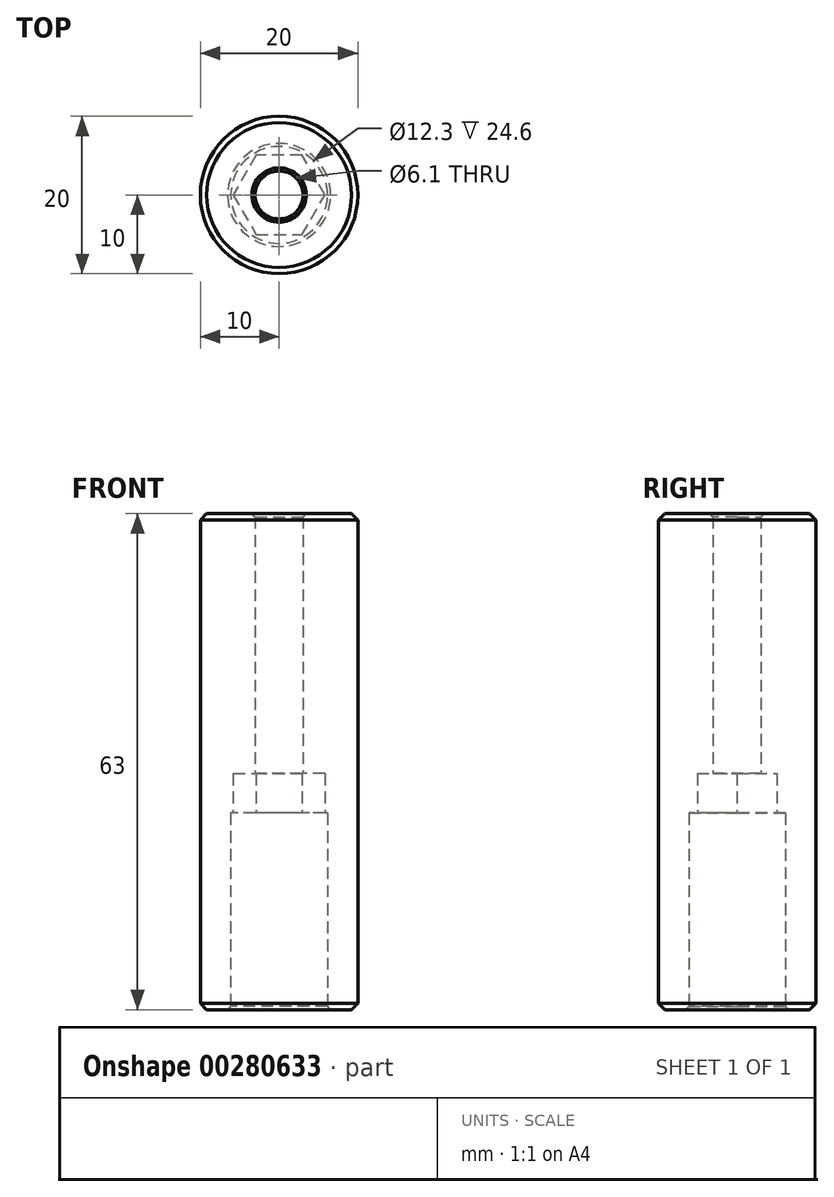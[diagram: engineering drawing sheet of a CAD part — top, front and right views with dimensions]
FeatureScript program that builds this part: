
annotation { "Feature Type Name" : "Feature", "Feature Type Description" : "" }
export const myFeature = defineFeature(function(context is Context, id is Id, definition is map)
    precondition{}
    {
        {
            var Q0;
            Q0=qCreatedBy(makeId("Top.planeOp"),FACE);
            var sketch = newSketch(context, id + "F0", { "sketchPlane" : qUnion([Q0])});
            skCircle(sketch, "E0", {"center": v(0, 0) * mm, "radius": 10 * mm});
            skCircle(sketch, "E1", {"center": v(0, 0) * mm, "radius": 6.15 * mm});
            skSolve(sketch);
        }
        {
            var Q0;
            Q0 = qSketchRegion(id + "F0", true);
            extrude(context, id + "F1", {"entities" : qUnion([Q0]), "depth" : 25 * mm});
        }
        {
            var Q0;
            Q0=makeQuery(id+"F1.opExtrude","CAP_FACE",FACE,{"disambiguationData":[OSD([sQuery(id+"F0.wireOp",EDGE,"E0"),sQuery(id+"F0.wireOp",EDGE,"E1")])],"isStart":false});
            var sketch = newSketch(context, id + "F2", { "sketchPlane" : qUnion([Q0])});
            skCircle(sketch, "E2.0", {"center": v(0, 0) * mm, "radius": 10 * mm});
            skSolve(sketch);
        }
        {
            var Q0;
            Q0 = qSketchRegion(id + "F2", true);
            extrude(context, id + "F3", {"entities" : qUnion([Q0]), "operationType" : NewBodyOperationType.ADD, "depth" : 38 * mm});
        }
        {
            var Q0;
            Q0=makeQuery(id+"F3.opExtrude","CAP_FACE",FACE,{"disambiguationData":[OSD([sQuery(id+"F2.wireOp",EDGE,"E2.0")])],"isStart":true});
            var sketch = newSketch(context, id + "F4", { "sketchPlane" : qUnion([Q0])});
            skCircle(sketch, "E3.cCircle", {"center": v(0, 0) * mm, "radius": 5.05 * mm, "construction": true});
            skLineSegment(sketch, "E3.0", {"start": v(2.92, -5.05) * mm, "end": v(-2.92, -5.05) * mm});
            skLineSegment(sketch, "E3.1", {"start": v(-2.92, -5.05) * mm, "end": v(-5.83, 0) * mm});
            skLineSegment(sketch, "E3.2", {"start": v(-5.83, 0) * mm, "end": v(-2.92, 5.05) * mm});
            skLineSegment(sketch, "E3.3", {"start": v(-2.92, 5.05) * mm, "end": v(2.92, 5.05) * mm});
            skLineSegment(sketch, "E3.4", {"start": v(2.92, 5.05) * mm, "end": v(5.83, 0) * mm});
            skLineSegment(sketch, "E3.5", {"start": v(5.83, 0) * mm, "end": v(2.92, -5.05) * mm});
            skPoint(sketch, "E3.0.midPoint", {"position": v(0, -5.05) * mm});
            skSolve(sketch);
        }
        {
            var Q0;
            Q0 = qSketchRegion(id + "F4", true);
            extrude(context, id + "F5", {"entities" : qUnion([Q0]), "operationType" : NewBodyOperationType.REMOVE, "oppositeDirection" : true, "depth" : 5 * mm});
        }
        {
            var Q0;
            Q0=makeQuery(id+"F5.boolean.opBoolean","COPY",FACE,{"derivedFrom":makeQuery(id+"F5.opExtrude","CAP_FACE",FACE,{"disambiguationData":[OSD([sQuery(id+"F4.wireOp",EDGE,"E3.0"),sQuery(id+"F4.wireOp",EDGE,"E3.1"),sQuery(id+"F4.wireOp",EDGE,"E3.2"),sQuery(id+"F4.wireOp",EDGE,"E3.3"),sQuery(id+"F4.wireOp",EDGE,"E3.4"),sQuery(id+"F4.wireOp",EDGE,"E3.5")])],"isStart":false})});
            var sketch = newSketch(context, id + "F6", { "sketchPlane" : qUnion([Q0])});
            skCircle(sketch, "E4", {"center": v(0, 0) * mm, "radius": 3.05 * mm});
            skSolve(sketch);
        }
        {
            var Q0;
            Q0 = qSketchRegion(id + "F6", true);
            extrude(context, id + "F7", {"entities" : qUnion([Q0]), "operationType" : NewBodyOperationType.REMOVE, "oppositeDirection" : true, "depth" : 50 * mm});
        }
        {
            var Q0;
            Q0=makeQuery(id+"F1.opExtrude","CAP_EDGE",EDGE,{"disambiguationData":[OSD([sQuery(id+"F0.wireOp",EDGE,"E0")])],"isStart":true});
            var Q1;
            Q1=makeQuery(id+"F3.opExtrude","CAP_EDGE",EDGE,{"disambiguationData":[OSD([sQuery(id+"F2.wireOp",EDGE,"E2.0")])],"isStart":false});
            chamfer(context, id + "F8", {"entities" : qUnion([Q0, Q1]), "width" : 0.8 * mm, "tangentPropagation" : true});
        }
        {
            var Q0;
            Q0=makeQuery(id+"F7.boolean.opBoolean","INTERSECT",EDGE,{"derivedFrom":[makeQuery(id+"F3.opExtrude","CAP_FACE",FACE,{"disambiguationData":[OSD([sQuery(id+"F2.wireOp",EDGE,"E2.0")])],"isStart":false}),makeQuery(id+"F7.opExtrude","SWEPT_FACE",FACE,{"disambiguationData":[OSD([sQuery(id+"F6.wireOp",EDGE,"E4")])]})]});
            chamfer(context, id + "F9", {"entities" : qUnion([Q0]), "width" : 0.4 * mm, "tangentPropagation" : true});
        }
        {
            var Q0;
            Q0=makeQuery(id+"F1.opExtrude","CAP_EDGE",EDGE,{"disambiguationData":[OSD([sQuery(id+"F0.wireOp",EDGE,"E1")])],"isStart":true});
            chamfer(context, id + "F10", {"entities" : qUnion([Q0]), "width" : 0.4 * mm, "tangentPropagation" : true});
        }
    });
